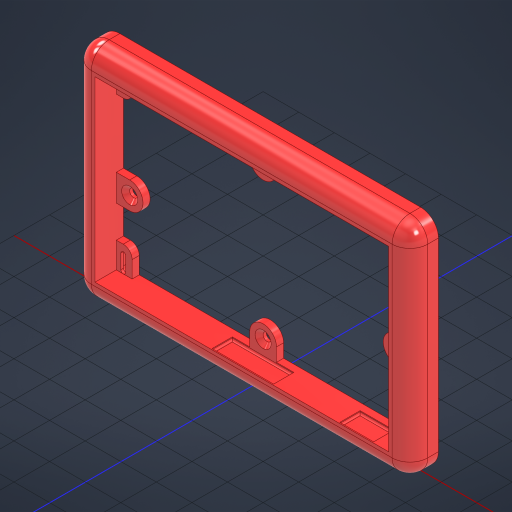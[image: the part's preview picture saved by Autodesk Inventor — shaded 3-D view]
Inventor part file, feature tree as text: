
AUTODESK INVENTOR PART (.ipt)
format: ipt  version: 2023.2 (Build 272271030, 271C)  size: 461,824 bytes
history: native  units: mm
features: extrude x5, fillet x3, sketch x2, projected_geometry x1
ambient origin geometry x8: Origin, YZ Plane, XZ Plane, XY Plane, X Axis, Y Axis, Z Axis, Center Point
bodies: Volumenkörper1 (feature_tree)
feature tree (11):
  sketch  "Skizze1"  dims[d0=100.0mm d1=165.0mm]
  extrude  "Extrusion1"  Depth=165.0mm
  extrude  "Extrusion2"  Depth=12.0mm TaperAngle=0.0deg
  fillet  "Rundung1"  Radius=4.0mm
  fillet  "Rundung2"  Radius=3.2mm
  extrude  "Extrusion3"  Depth=10.0mm
  fillet  "Rundung3"  Radius=10.0mm
  extrude  "Extrusion4"  Depth=9.0mm
  extrude  "Extrusion5"  Depth=19.0mm
  sketch  "Skizze2"  dims[d2=12.0mm d9=12.0mm d10=0.0mm d11=4.0mm d12=0.0mm d13=3.2mm d14=10.0mm d15=10.0mm d16=9.0mm d17=19.0mm d18=1.5mm d19=11.4mm d20=0.0mm d21=1.0mm d23=2.7mm d24=2.7mm d25=10.8mm d26=10.8mm d27=2.7mm d28=2.7mm d30=10.8mm d31=89.2mm d32=157.2mm d33=10.8mm d34=5.0mm d36=2.5mm d37=0.0mm d38=15.0mm d39=15.0mm d41=4.5mm d43=9.0mm d44=3.0mm d45=-7.853982mm d46=10.0mm d49=34.6mm d50=5.0mm]
  projected_geometry  "Projizierte Kontur1"
